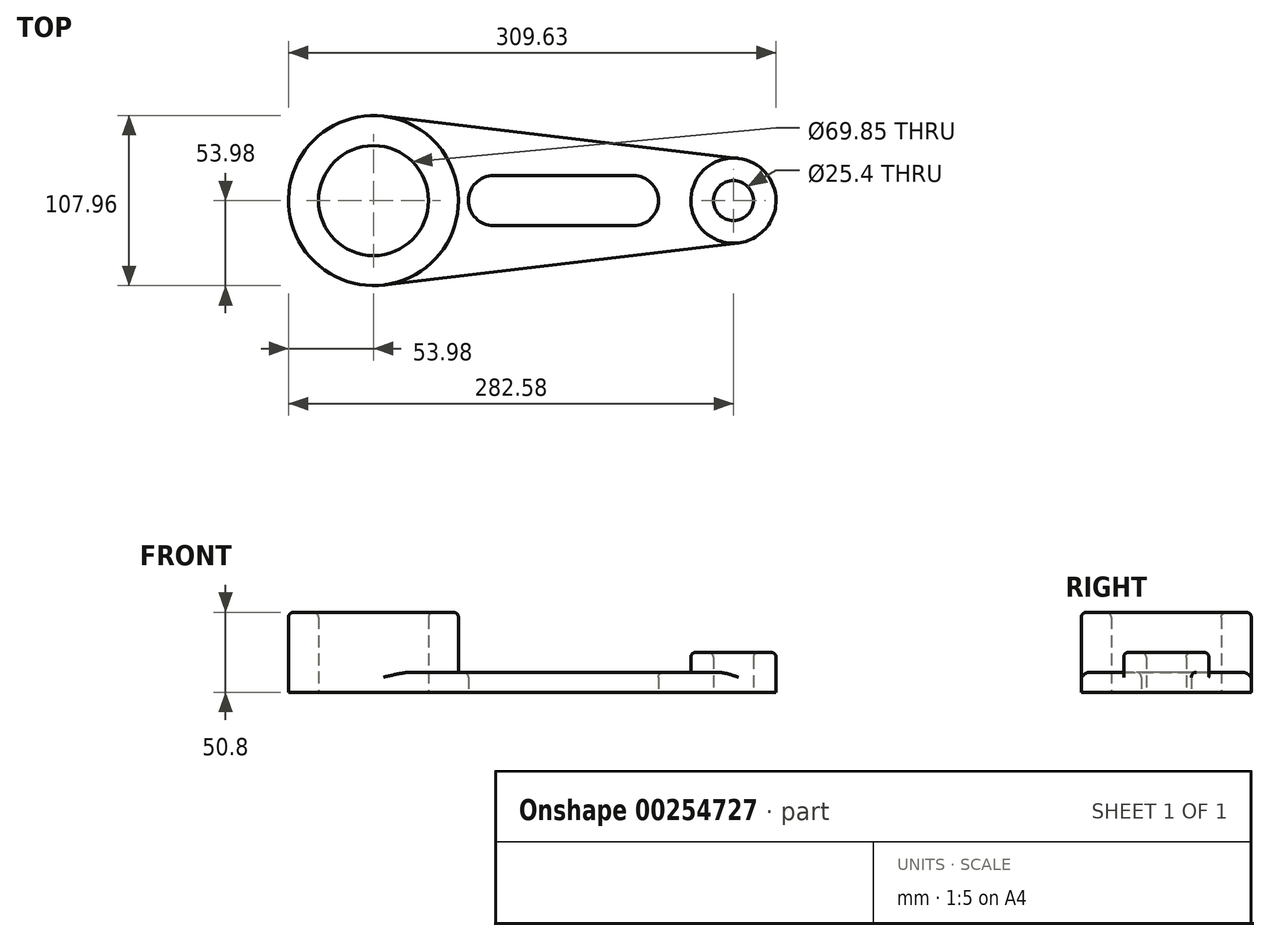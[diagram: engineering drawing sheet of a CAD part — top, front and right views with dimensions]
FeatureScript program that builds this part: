
annotation { "Feature Type Name" : "Feature", "Feature Type Description" : "" }
export const myFeature = defineFeature(function(context is Context, id is Id, definition is map)
    precondition{}
    {
        {
            var Q0;
            Q0=qCreatedBy(makeId("Top.planeOp"),FACE);
            var sketch = newSketch(context, id + "F0", { "sketchPlane" : qUnion([Q0])});
            skCircle(sketch, "E0", {"center": v(0, 0) * mm, "radius": 12.7 * mm});
            skCircle(sketch, "E1", {"center": v(0, 0) * mm, "radius": 27.05 * mm});
            skCircle(sketch, "E2", {"center": v(-63.5, 0) * mm, "radius": 15.88 * mm});
            skCircle(sketch, "E3", {"center": v(-152.4, 0) * mm, "radius": 15.88 * mm});
            skLineSegment(sketch, "E4", {"start": v(-152.4, 15.88) * mm, "end": v(-63.5, 15.88) * mm});
            skLineSegment(sketch, "E5", {"start": v(-152.4, -15.88) * mm, "end": v(-63.5, -15.88) * mm});
            skCircle(sketch, "E6", {"center": v(-228.6, 0) * mm, "radius": 34.93 * mm});
            skCircle(sketch, "E7", {"center": v(-228.6, 0) * mm, "radius": 53.98 * mm});
            skLineSegment(sketch, "E8", {"start": v(-222.24, 53.6) * mm, "end": v(3.19, 26.86) * mm});
            skLineSegment(sketch, "E9", {"start": v(-222.24, -53.6) * mm, "end": v(3.19, -26.86) * mm});
            skSolve(sketch);
        }
        {
            var Q0;
            Q0=makeQuery(id+"F0.imprint","IMPRINT",FACE,{"disambiguationData":[TD([[makeQuery(id+"F0.imprint","IMPRINT",EDGE,{"derivedFrom":sQuery(id+"F0.wireOp",EDGE,"E6")}),-1.0]])]});
            extrude(context, id + "F1", {"entities" : qUnion([Q0]), "depth" : 50.8 * mm});
        }
        {
            var Q0;
            {var subQ0=sQuery(id+"F0.wireOp",EDGE,"E4");Q0=makeQuery(id+"F0.imprint","IMPRINT",FACE,{"disambiguationData":[TD([[makeQuery(id+"F0.imprint","IMPRINT",EDGE,{"derivedFrom":subQ0}),1.0]])]});}
            extrude(context, id + "F2", {"entities" : qUnion([Q0]), "operationType" : NewBodyOperationType.ADD, "depth" : 12.7 * mm});
        }
        {
            var Q0;
            Q0=makeQuery(id+"F0.imprint","IMPRINT",FACE,{"disambiguationData":[TD([[makeQuery(id+"F0.imprint","IMPRINT",EDGE,{"derivedFrom":sQuery(id+"F0.wireOp",EDGE,"E0")}),-1.0]])]});
            extrude(context, id + "F3", {"entities" : qUnion([Q0]), "operationType" : NewBodyOperationType.ADD, "depth" : 25.4 * mm});
        }
        {
            var Q0;
            Q0=makeQuery(id+"F1.opExtrude","CAP_EDGE",EDGE,{"disambiguationData":[OSD([sQuery(id+"F0.wireOp",EDGE,"E7")])],"isStart":false});
            var Q1;
            Q1=makeQuery(id+"F1.opExtrude","CAP_EDGE",EDGE,{"disambiguationData":[OSD([sQuery(id+"F0.wireOp",EDGE,"E6")])],"isStart":false});
            var Q2;
            Q2=makeQuery(id+"F2.opExtrude","CAP_EDGE",EDGE,{"disambiguationData":[OSD([sQuery(id+"F0.wireOp",EDGE,"E4")])],"isStart":false});
            var Q3;
            Q3=makeQuery(id+"F2.opExtrude","CAP_EDGE",EDGE,{"disambiguationData":[OSD([sQuery(id+"F0.wireOp",EDGE,"E3")])],"isStart":false});
            var Q4;
            Q4=makeQuery(id+"F2.opExtrude","CAP_EDGE",EDGE,{"disambiguationData":[OSD([sQuery(id+"F0.wireOp",EDGE,"E5")])],"isStart":false});
            var Q5;
            Q5=makeQuery(id+"F2.opExtrude","CAP_EDGE",EDGE,{"disambiguationData":[OSD([sQuery(id+"F0.wireOp",EDGE,"E2")])],"isStart":false});
            var Q6;
            Q6=makeQuery(id+"F2.opExtrude","CAP_EDGE",EDGE,{"disambiguationData":[OSD([sQuery(id+"F0.wireOp",EDGE,"E8")])],"isStart":false});
            var Q7;
            Q7=makeQuery(id+"F2.opExtrude","CAP_EDGE",EDGE,{"disambiguationData":[OSD([sQuery(id+"F0.wireOp",EDGE,"E9")])],"isStart":false});
            var Q8;
            Q8=makeQuery(id+"F3.opExtrude","CAP_EDGE",EDGE,{"disambiguationData":[OSD([sQuery(id+"F0.wireOp",EDGE,"E1")])],"isStart":false});
            var Q9;
            Q9=makeQuery(id+"F3.opExtrude","CAP_EDGE",EDGE,{"disambiguationData":[OSD([sQuery(id+"F0.wireOp",EDGE,"E0")])],"isStart":false});
            fillet(context, id + "F4", {"entities" : qUnion([Q0, Q1, Q2, Q3, Q4, Q5, Q6, Q7, Q8, Q9]), "radius" : 3.17 * mm, "tangentPropagation" : true, "allowEdgeOverflow" : false});
        }
    });
